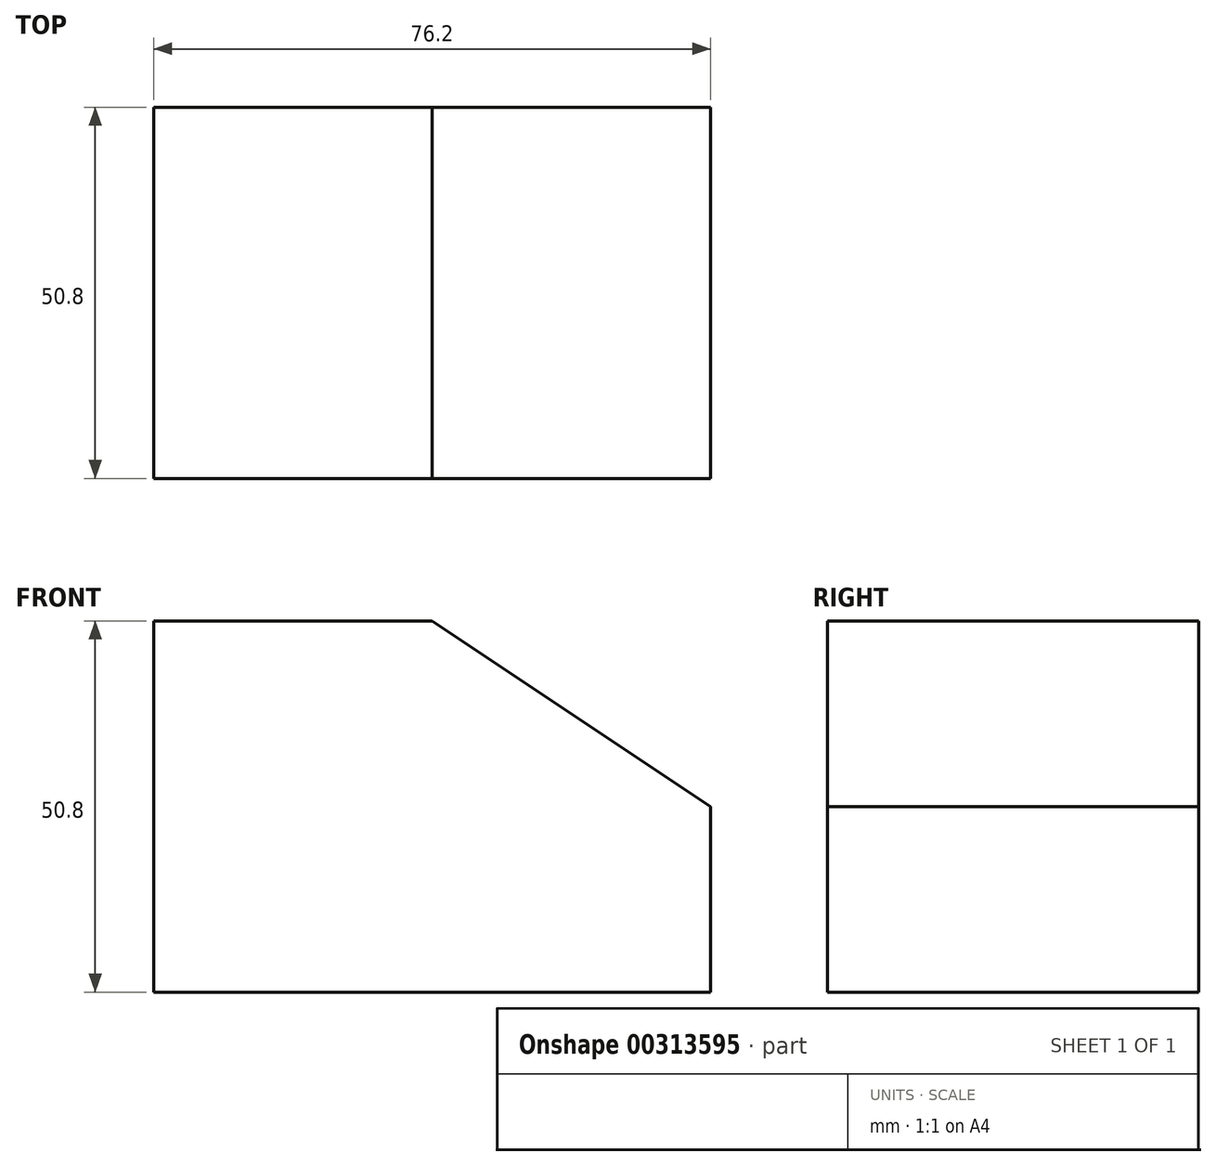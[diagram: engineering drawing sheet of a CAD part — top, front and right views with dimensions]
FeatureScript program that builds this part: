
annotation { "Feature Type Name" : "Feature", "Feature Type Description" : "" }
export const myFeature = defineFeature(function(context is Context, id is Id, definition is map)
    precondition{}
    {
        {
            var Q0;
            Q0=qCreatedBy(makeId("Front.planeOp"),FACE);
            var sketch = newSketch(context, id + "F0", { "sketchPlane" : qUnion([Q0])});
            skLineSegment(sketch, "E0", {"start": v(-32.57, -39.55) * mm, "end": v(43.63, -39.55) * mm});
            skLineSegment(sketch, "E1", {"start": v(43.63, -39.55) * mm, "end": v(43.63, -14.15) * mm});
            skLineSegment(sketch, "E2", {"start": v(43.63, -14.15) * mm, "end": v(5.53, 11.25) * mm});
            skLineSegment(sketch, "E3", {"start": v(5.53, 11.25) * mm, "end": v(-32.57, 11.25) * mm});
            skLineSegment(sketch, "E4", {"start": v(-32.57, 11.25) * mm, "end": v(-32.57, -39.55) * mm});
            skSolve(sketch);
        }
        {
            var Q0;
            Q0=makeQuery(id+"F0.imprint","IMPRINT",FACE,{"disambiguationData":[TD([[makeQuery(id+"F0.imprint","IMPRINT",EDGE,{"derivedFrom":sQuery(id+"F0.wireOp",EDGE,"E0")}),1.0]])]});
            extrude(context, id + "F1", {"entities" : qUnion([Q0]), "depth" : 50.8 * mm});
        }
    });
